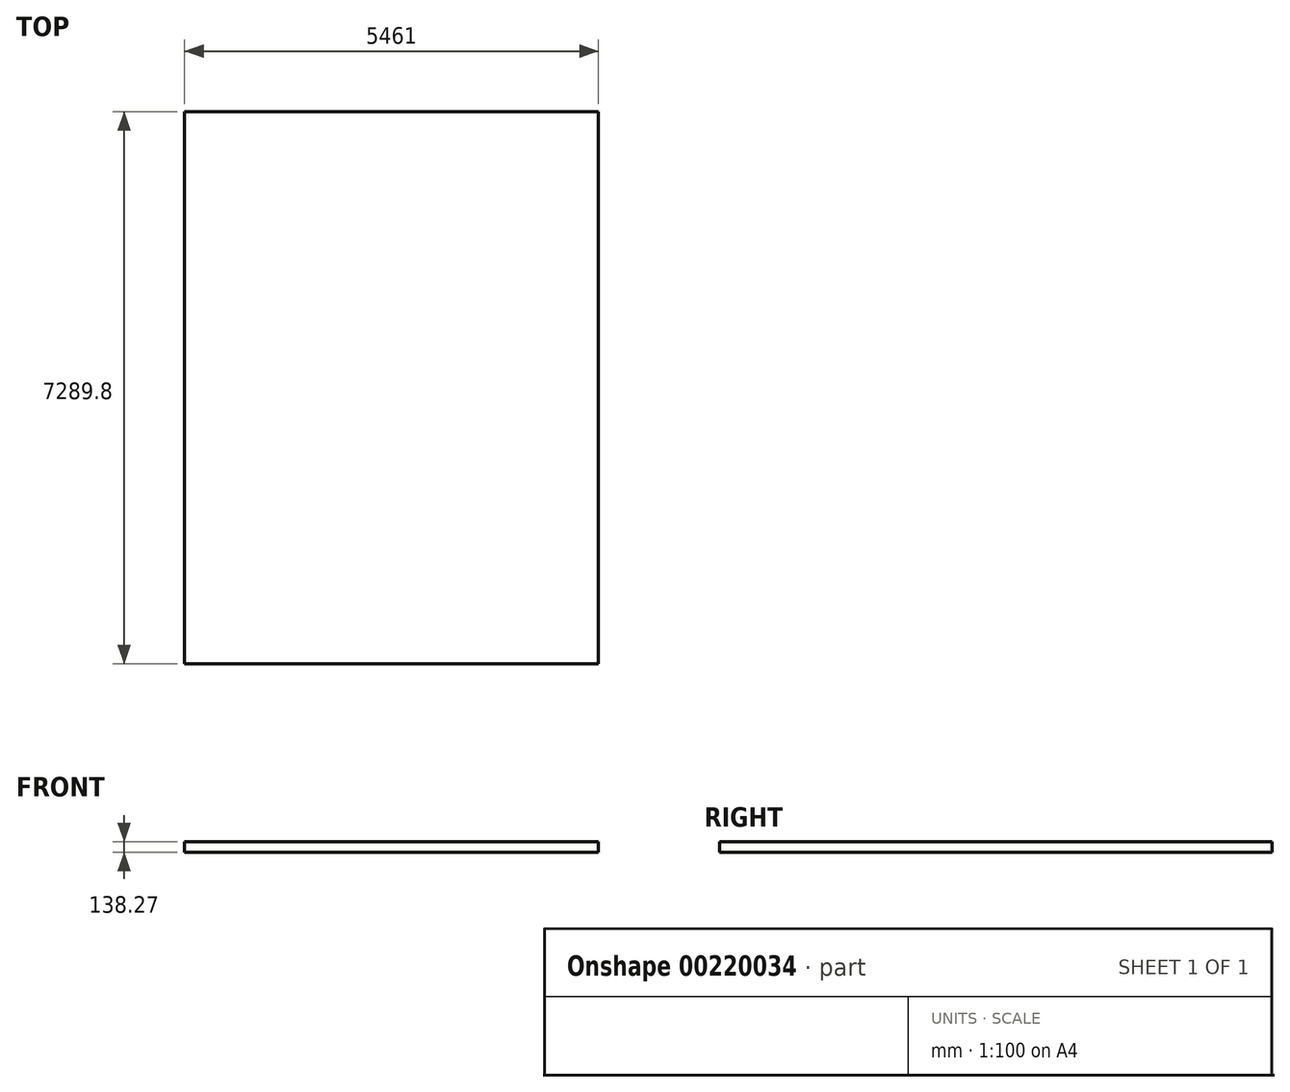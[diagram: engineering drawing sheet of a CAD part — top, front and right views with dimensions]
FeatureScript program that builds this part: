
annotation { "Feature Type Name" : "Feature", "Feature Type Description" : "" }
export const myFeature = defineFeature(function(context is Context, id is Id, definition is map)
    precondition{}
    {
        {
            var Q0;
            Q0=qCreatedBy(makeId("Top.planeOp"),FACE);
            var sketch = newSketch(context, id + "F0", { "sketchPlane" : qUnion([Q0])});
            skLineSegment(sketch, "E0.bottom", {"start": v(0, 0) * mm, "end": v(-5461, 0) * mm});
            skLineSegment(sketch, "E0.top", {"start": v(0, 7289.8) * mm, "end": v(-5461, 7289.8) * mm});
            skLineSegment(sketch, "E0.left", {"start": v(0, 0) * mm, "end": v(0, 7289.8) * mm});
            skLineSegment(sketch, "E0.right", {"start": v(-5461, 0) * mm, "end": v(-5461, 7289.8) * mm});
            skSolve(sketch);
        }
        {
            var Q0;
            Q0=makeQuery(id+"F0.imprint","IMPRINT",FACE,{"disambiguationData":[TD([[makeQuery(id+"F0.imprint","IMPRINT",EDGE,{"derivedFrom":sQuery(id+"F0.wireOp",EDGE,"E0.bottom")}),-1.0]])]});
            extrude(context, id + "F1", {"entities" : qUnion([Q0]), "depth" : 138.27 * mm});
        }
    });
